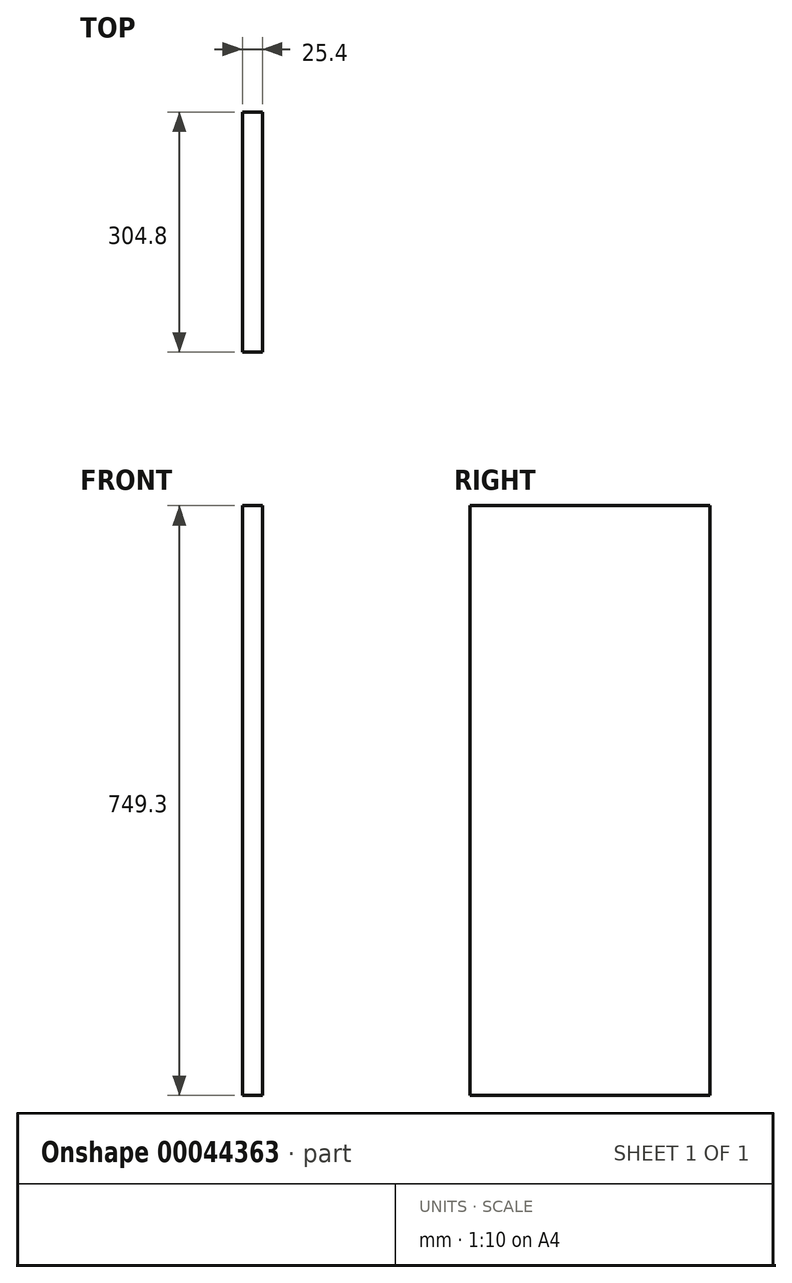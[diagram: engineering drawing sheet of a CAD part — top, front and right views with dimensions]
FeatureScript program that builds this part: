
annotation { "Feature Type Name" : "Feature", "Feature Type Description" : "" }
export const myFeature = defineFeature(function(context is Context, id is Id, definition is map)
    precondition{}
    {
        {
            var Q0;
            Q0=qCreatedBy(makeId("Front.planeOp"),FACE);
            var sketch = newSketch(context, id + "F0", { "sketchPlane" : qUnion([Q0])});
            skLineSegment(sketch, "E0.rect.bottom", {"start": v(12.7, 374.65) * mm, "end": v(-12.7, 374.65) * mm});
            skLineSegment(sketch, "E0.rect.top", {"start": v(12.7, -374.65) * mm, "end": v(-12.7, -374.65) * mm});
            skLineSegment(sketch, "E0.rect.left", {"start": v(12.7, 374.65) * mm, "end": v(12.7, -374.65) * mm});
            skLineSegment(sketch, "E0.rect.right", {"start": v(-12.7, 374.65) * mm, "end": v(-12.7, -374.65) * mm});
            skPoint(sketch, "E0.rect.middle", {"position": v(0, 0) * mm});
            skSolve(sketch);
        }
        {
            var Q0;
            Q0 = qSketchRegion(id + "F0", true);
            extrude(context, id + "F1", {"entities" : qUnion([Q0]), "endBound" : BoundingType.SYMMETRIC, "depth" : 304.8 * mm});
        }
    });
